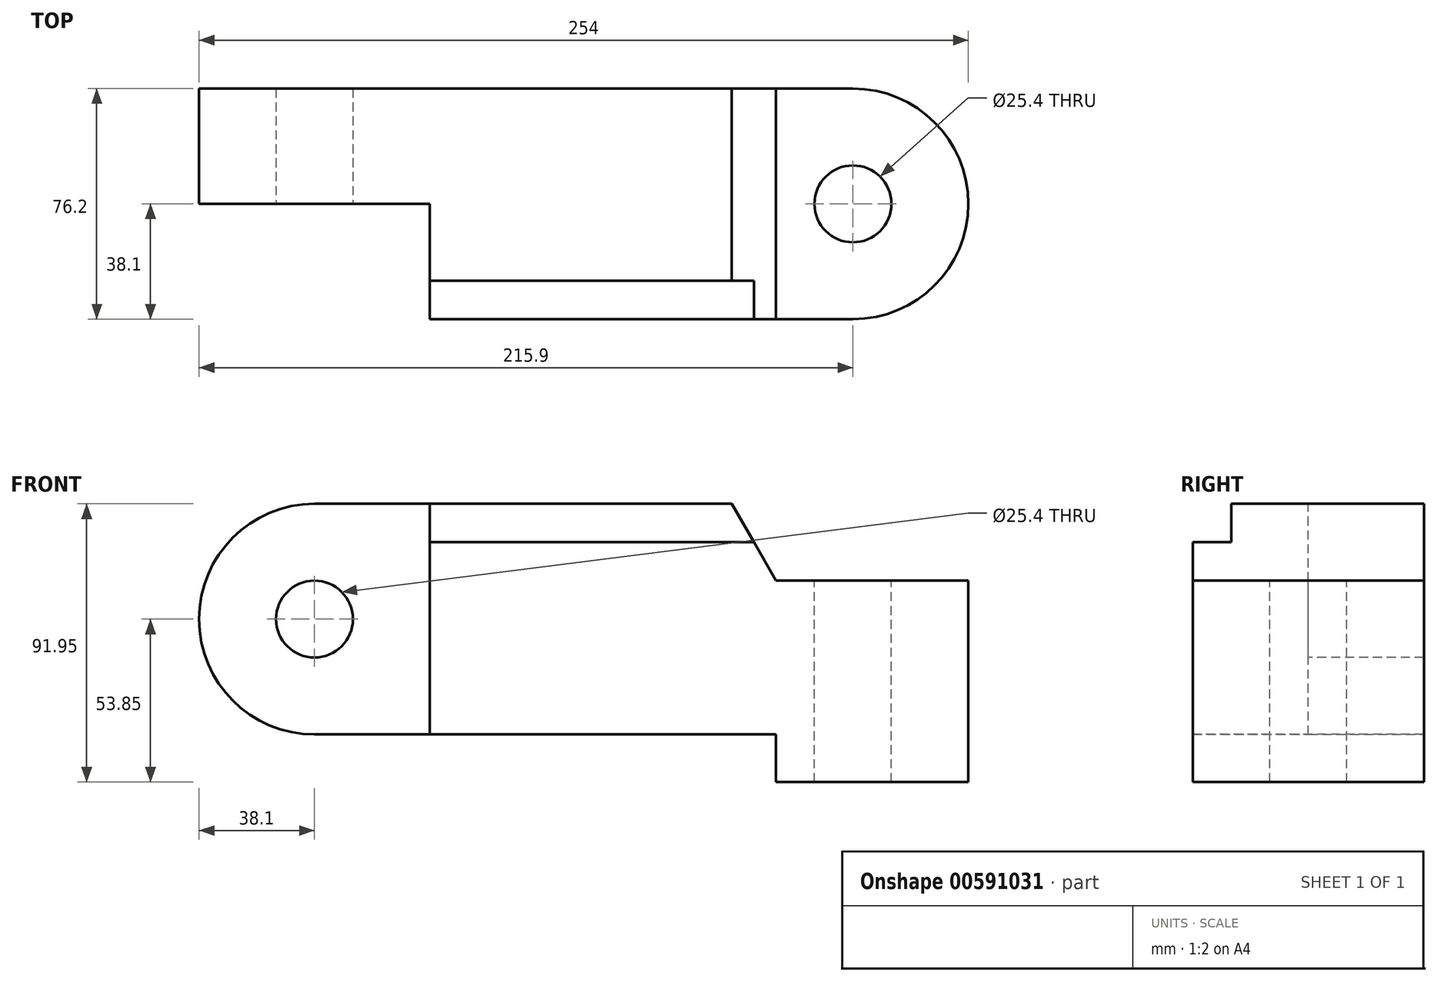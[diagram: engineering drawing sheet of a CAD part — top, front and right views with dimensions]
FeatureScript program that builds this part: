
annotation { "Feature Type Name" : "Feature", "Feature Type Description" : "" }
export const myFeature = defineFeature(function(context is Context, id is Id, definition is map)
    precondition{}
    {
        {
            var Q0;
            Q0=qCreatedBy(makeId("Top.planeOp"),FACE);
            var sketch = newSketch(context, id + "F0", { "sketchPlane" : qUnion([Q0])});
            skLineSegment(sketch, "E0.bottom", {"start": v(88.9, -38.1) * mm, "end": v(-88.9, -38.1) * mm});
            skLineSegment(sketch, "E0.top", {"start": v(88.9, 38.1) * mm, "end": v(-88.9, 38.1) * mm});
            skLineSegment(sketch, "E0.left", {"start": v(88.9, -38.1) * mm, "end": v(88.9, 38.1) * mm});
            skLineSegment(sketch, "E0.right", {"start": v(-88.9, -38.1) * mm, "end": v(-88.9, 38.1) * mm});
            skPoint(sketch, "E0.middle", {"position": v(0, 0) * mm});
            skSolve(sketch);
        }
        {
            var Q0;
            Q0=makeQuery(id+"F0.imprint","IMPRINT",FACE,{"disambiguationData":[TD([[makeQuery(id+"F0.imprint","IMPRINT",EDGE,{"derivedFrom":sQuery(id+"F0.wireOp",EDGE,"E0.bottom")}),-1.0]])]});
            extrude(context, id + "F1", {"entities" : qUnion([Q0]), "depth" : 76.2 * mm, "offsetDistance" : 25.4 * mm});
        }
        {
            var Q0;
            Q0=makeQuery(id+"F1.opExtrude","CAP_FACE",FACE,{"disambiguationData":[OSD([sQuery(id+"F0.wireOp",EDGE,"E0.bottom"),sQuery(id+"F0.wireOp",EDGE,"E0.top"),sQuery(id+"F0.wireOp",EDGE,"E0.left"),sQuery(id+"F0.wireOp",EDGE,"E0.right")])],"isStart":false});
            var sketch = newSketch(context, id + "F2", { "sketchPlane" : qUnion([Q0])});
            skLineSegment(sketch, "E1.bottom", {"start": v(-88.9, -38.1) * mm, "end": v(-50.8, -38.1) * mm});
            skLineSegment(sketch, "E1.top", {"start": v(-88.9, 0) * mm, "end": v(-50.8, 0) * mm});
            skLineSegment(sketch, "E1.left", {"start": v(-88.9, -38.1) * mm, "end": v(-88.9, 0) * mm});
            skLineSegment(sketch, "E1.right", {"start": v(-50.8, -38.1) * mm, "end": v(-50.8, 0) * mm});
            skSolve(sketch);
        }
        {
            var Q0;
            Q0=makeQuery(id+"F2.imprint","IMPRINT",FACE,{"disambiguationData":[TD([[makeQuery(id+"F2.imprint","IMPRINT",EDGE,{"derivedFrom":sQuery(id+"F2.wireOp",EDGE,"E1.bottom")}),-1.0]])]});
            extrude(context, id + "F3", {"entities" : qUnion([Q0]), "operationType" : NewBodyOperationType.REMOVE, "oppositeDirection" : true, "depth" : 76.2 * mm, "offsetDistance" : 25.4 * mm});
        }
        {
            var Q0;
            Q0=makeQuery(id+"F1.opExtrude","CAP_FACE",FACE,{"disambiguationData":[OSD([sQuery(id+"F0.wireOp",EDGE,"E0.bottom"),sQuery(id+"F0.wireOp",EDGE,"E0.top"),sQuery(id+"F0.wireOp",EDGE,"E0.left"),sQuery(id+"F0.wireOp",EDGE,"E0.right")])],"isStart":false});
            var sketch = newSketch(context, id + "F4", { "sketchPlane" : qUnion([Q0])});
            skLineSegment(sketch, "E2.bottom", {"start": v(88.9, -38.1) * mm, "end": v(63.5, -38.1) * mm});
            skLineSegment(sketch, "E2.top", {"start": v(88.9, 38.1) * mm, "end": v(63.5, 38.1) * mm});
            skLineSegment(sketch, "E2.left", {"start": v(88.9, -38.1) * mm, "end": v(88.9, 38.1) * mm});
            skLineSegment(sketch, "E2.right", {"start": v(63.5, -38.1) * mm, "end": v(63.5, 38.1) * mm});
            skSolve(sketch);
        }
        {
            var Q0;
            Q0=makeQuery(id+"F4.imprint","IMPRINT",FACE,{"disambiguationData":[TD([[makeQuery(id+"F4.imprint","IMPRINT",EDGE,{"derivedFrom":sQuery(id+"F4.wireOp",EDGE,"E2.bottom")}),-1.0]])]});
            extrude(context, id + "F5", {"entities" : qUnion([Q0]), "operationType" : NewBodyOperationType.REMOVE, "oppositeDirection" : true, "depth" : 25.4 * mm, "offsetDistance" : 25.4 * mm});
        }
        {
            var Q0;
            Q0=makeQuery(id+"F1.opExtrude","CAP_FACE",FACE,{"disambiguationData":[OSD([sQuery(id+"F0.wireOp",EDGE,"E0.bottom"),sQuery(id+"F0.wireOp",EDGE,"E0.top"),sQuery(id+"F0.wireOp",EDGE,"E0.left"),sQuery(id+"F0.wireOp",EDGE,"E0.right")])],"isStart":true});
            var sketch = newSketch(context, id + "F6", { "sketchPlane" : qUnion([Q0])});
            skLineSegment(sketch, "E3.bottom", {"start": v(88.9, -38.1) * mm, "end": v(63.5, -38.1) * mm});
            skLineSegment(sketch, "E3.top", {"start": v(88.9, 38.1) * mm, "end": v(63.5, 38.1) * mm});
            skLineSegment(sketch, "E3.left", {"start": v(88.9, -38.1) * mm, "end": v(88.9, 38.1) * mm});
            skLineSegment(sketch, "E3.right", {"start": v(63.5, -38.1) * mm, "end": v(63.5, 38.1) * mm});
            skSolve(sketch);
        }
        {
            var Q0;
            Q0=makeQuery(id+"F6.imprint","IMPRINT",FACE,{"disambiguationData":[TD([[makeQuery(id+"F6.imprint","IMPRINT",EDGE,{"derivedFrom":sQuery(id+"F6.wireOp",EDGE,"E3.bottom")}),-1.0]])]});
            extrude(context, id + "F7", {"entities" : qUnion([Q0]), "operationType" : NewBodyOperationType.ADD, "depth" : 15.75 * mm, "offsetDistance" : 25.4 * mm});
        }
        {
            var Q0;
            Q0=makeQuery(id+"F1.opExtrude","SWEPT_FACE",FACE,{"disambiguationData":[OSD([sQuery(id+"F0.wireOp",EDGE,"E0.right")])]});
            var sketch = newSketch(context, id + "F8", { "sketchPlane" : qUnion([Q0])});
            skLineSegment(sketch, "E4", {"start": v(-38.1, 38.1) * mm, "end": v(0, 38.1) * mm});
            skSolve(sketch);
        }
        {
            var Q0;
            {var subQ0=sQuery(id+"F8.wireOp",EDGE,"E4");Q0=makeQuery(id+"F8.imprint","IMPRINT",FACE,{"disambiguationData":[TD([[makeQuery(id+"F8.imprint","IMPRINT",EDGE,{"derivedFrom":subQ0}),1.0]])]});}
            var Q1;
            Q1=sQuery(id+"F8.wireOp",EDGE,"E4");
            revolve(context, id + "F9", {"operationType" : NewBodyOperationType.ADD, "entities" : qUnion([Q0]), "axis" : qUnion([Q1]), "revolveType" : RevolveType.FULL});
        }
        {
            var Q0;
            Q0=makeQuery(id+"F7.boolean.opBoolean","MERGE",FACE,{"derivedFrom":[makeQuery(id+"F1.opExtrude","SWEPT_FACE",FACE,{"disambiguationData":[OSD([sQuery(id+"F0.wireOp",EDGE,"E0.left")])]}),makeQuery(id+"F7.opExtrude","SWEPT_FACE",FACE,{"disambiguationData":[OSD([sQuery(id+"F6.wireOp",EDGE,"E3.left")])]})]});
            var sketch = newSketch(context, id + "F10", { "sketchPlane" : qUnion([Q0])});
            skLineSegment(sketch, "E5", {"start": v(0, 50.8) * mm, "end": v(0, -15.75) * mm});
            skSolve(sketch);
        }
        {
            var Q0;
            {var subQ0=sQuery(id+"F10.wireOp",EDGE,"E5");Q0=makeQuery(id+"F10.imprint","IMPRINT",FACE,{"disambiguationData":[TD([[makeQuery(id+"F10.imprint","IMPRINT",EDGE,{"derivedFrom":subQ0}),1.0]])]});}
            var Q1;
            Q1=sQuery(id+"F10.wireOp",EDGE,"E5");
            revolve(context, id + "F11", {"operationType" : NewBodyOperationType.ADD, "entities" : qUnion([Q0]), "axis" : qUnion([Q1]), "revolveType" : RevolveType.FULL});
        }
        {
            var Q0;
            Q0=makeQuery(id+"F7.boolean.opBoolean","MERGE",FACE,{"derivedFrom":[makeQuery(id+"F1.opExtrude","SWEPT_FACE",FACE,{"disambiguationData":[OSD([sQuery(id+"F0.wireOp",EDGE,"E0.bottom")])]}),makeQuery(id+"F7.opExtrude","SWEPT_FACE",FACE,{"disambiguationData":[OSD([sQuery(id+"F6.wireOp",EDGE,"E3.top")])]})]});
            var sketch = newSketch(context, id + "F12", { "sketchPlane" : qUnion([Q0])});
            skLineSegment(sketch, "E6", {"start": v(63.5, 50.8) * mm, "end": v(48.84, 76.2) * mm});
            skSolve(sketch);
        }
        {
            var Q0;
            Q0 = qSketchRegion(id + "F12", true);
            var Q1;
            {var subQ0=sQuery(id+"F12.wireOp",EDGE,"E6");Q1=makeQuery(id+"F12.imprint","IMPRINT",FACE,{"disambiguationData":[TD([[makeQuery(id+"F12.imprint","IMPRINT",EDGE,{"derivedFrom":subQ0}),-1.0]])]});}
            extrude(context, id + "F13", {"entities" : qUnion([Q0, Q1]), "operationType" : NewBodyOperationType.REMOVE, "oppositeDirection" : true, "depth" : 76.2 * mm, "offsetDistance" : 25.4 * mm});
        }
        {
            var Q0;
            {var subQ0=sQuery(id+"F4.wireOp",EDGE,"E2.left");Q0=makeQuery(id+"F11.boolean.opBoolean","MERGE",FACE,{"derivedFrom":[makeQuery(id+"F5.boolean.opBoolean","COPY",FACE,{"derivedFrom":makeQuery(id+"F5.opExtrude","CAP_FACE",FACE,{"disambiguationData":[OSD([sQuery(id+"F4.wireOp",EDGE,"E2.bottom"),sQuery(id+"F4.wireOp",EDGE,"E2.top"),subQ0,sQuery(id+"F4.wireOp",EDGE,"E2.right")])],"isStart":false})}),makeQuery(id+"F11.opRevolve","SWEPT_FACE",FACE,{"disambiguationData":[OSD([subQ0])]})]});}
            var sketch = newSketch(context, id + "F14", { "sketchPlane" : qUnion([Q0])});
            skLineSegment(sketch, "E7.bottom", {"start": v(63.5, -38.1) * mm, "end": v(88.9, -38.1) * mm});
            skLineSegment(sketch, "E7.top", {"start": v(63.5, 0) * mm, "end": v(88.9, 0) * mm});
            skLineSegment(sketch, "E7.left", {"start": v(63.5, -38.1) * mm, "end": v(63.5, 0) * mm});
            skLineSegment(sketch, "E7.right", {"start": v(88.9, -38.1) * mm, "end": v(88.9, 0) * mm});
            skCircle(sketch, "E8", {"center": v(88.9, 0) * mm, "radius": 12.7 * mm});
            skSolve(sketch);
        }
        {
            var Q0;
            {var subQ0=sQuery(id+"F14.wireOp",EDGE,"E7.right");var subQ1=sQuery(id+"F14.wireOp",EDGE,"E7.top");var subQ2=makeQuery(id+"F14.imprint","INTERSECT",VERTEX,{"derivedFrom":[subQ1,subQ0]});Q0=makeQuery(id+"F14.imprint","IMPRINT",FACE,{"disambiguationData":[TD([[makeQuery(id+"F14.imprint","IMPRINT",EDGE,{"disambiguationData":[TD([[subQ2,1.0]])],"derivedFrom":subQ1}),-1.0]])]});}
            var Q1;
            {var subQ0=sQuery(id+"F14.wireOp",EDGE,"E7.right");var subQ1=sQuery(id+"F14.wireOp",EDGE,"E7.top");var subQ2=makeQuery(id+"F14.imprint","INTERSECT",VERTEX,{"derivedFrom":[subQ1,subQ0]});Q1=makeQuery(id+"F14.imprint","IMPRINT",FACE,{"disambiguationData":[TD([[makeQuery(id+"F14.imprint","IMPRINT",EDGE,{"disambiguationData":[TD([[subQ2,1.0]])],"derivedFrom":subQ1}),1.0]])]});}
            extrude(context, id + "F15", {"entities" : qUnion([Q0, Q1]), "operationType" : NewBodyOperationType.REMOVE, "oppositeDirection" : true, "depth" : 101.6 * mm, "offsetDistance" : 25.4 * mm});
        }
        {
            var Q0;
            {var subQ0=sQuery(id+"F6.wireOp",EDGE,"E3.left");Q0=makeQuery(id+"F11.boolean.opBoolean","MERGE",FACE,{"derivedFrom":[makeQuery(id+"F7.opExtrude","CAP_FACE",FACE,{"disambiguationData":[OSD([sQuery(id+"F6.wireOp",EDGE,"E3.bottom"),sQuery(id+"F6.wireOp",EDGE,"E3.top"),subQ0,sQuery(id+"F6.wireOp",EDGE,"E3.right")])],"isStart":false}),makeQuery(id+"F11.opRevolve","SWEPT_FACE",FACE,{"disambiguationData":[OSD([subQ0])]})]});}
            var sketch = newSketch(context, id + "F16", { "sketchPlane" : qUnion([Q0])});
            skLineSegment(sketch, "E9", {"start": v(63.5, 28.4) * mm, "end": v(63.5, -28.4) * mm});
            skSolve(sketch);
        }
        {
            var Q0;
            Q0=makeQuery(id+"F16.imprint","IMPRINT",FACE,{"disambiguationData":[TD([[makeQuery(id+"F16.imprint","IMPRINT",EDGE,{"derivedFrom":sQuery(id+"F16.wireOp",EDGE,"E9")}),-1.0]])]});
            extrude(context, id + "F17", {"entities" : qUnion([Q0]), "operationType" : NewBodyOperationType.REMOVE, "oppositeDirection" : true, "depth" : 15.75 * mm, "offsetDistance" : 25.4 * mm});
        }
        {
            var Q0;
            {var subQ0=sQuery(id+"F2.wireOp",EDGE,"E1.top");Q0=makeQuery(id+"F9.boolean.opBoolean","MERGE",FACE,{"derivedFrom":[makeQuery(id+"F3.boolean.opBoolean","COPY",FACE,{"derivedFrom":makeQuery(id+"F3.opExtrude","SWEPT_FACE",FACE,{"disambiguationData":[OSD([subQ0])]})}),makeQuery(id+"F9.opRevolve","SWEPT_FACE",FACE,{"disambiguationData":[OSD([sQuery(id+"F0.wireOp",EDGE,"E0.right"),subQ0,sQuery(id+"F2.wireOp",EDGE,"E1.left")])]})]});}
            var sketch = newSketch(context, id + "F18", { "sketchPlane" : qUnion([Q0])});
            skLineSegment(sketch, "E10.bottom", {"start": v(-50.8, 76.2) * mm, "end": v(-88.9, 76.2) * mm});
            skLineSegment(sketch, "E10.top", {"start": v(-50.8, 38.1) * mm, "end": v(-88.9, 38.1) * mm});
            skLineSegment(sketch, "E10.left", {"start": v(-50.8, 76.2) * mm, "end": v(-50.8, 38.1) * mm});
            skLineSegment(sketch, "E10.right", {"start": v(-88.9, 76.2) * mm, "end": v(-88.9, 38.1) * mm});
            skCircle(sketch, "E11", {"center": v(-88.9, 38.1) * mm, "radius": 12.7 * mm});
            skSolve(sketch);
        }
        {
            var Q0;
            {var subQ0=sQuery(id+"F18.wireOp",EDGE,"E10.right");var subQ1=sQuery(id+"F18.wireOp",EDGE,"E10.top");var subQ2=makeQuery(id+"F18.imprint","INTERSECT",VERTEX,{"derivedFrom":[subQ1,subQ0]});Q0=makeQuery(id+"F18.imprint","IMPRINT",FACE,{"disambiguationData":[TD([[makeQuery(id+"F18.imprint","IMPRINT",EDGE,{"disambiguationData":[TD([[subQ2,1.0]])],"derivedFrom":subQ1}),-1.0]])]});}
            var Q1;
            {var subQ0=sQuery(id+"F18.wireOp",EDGE,"E10.right");var subQ1=sQuery(id+"F18.wireOp",EDGE,"E10.top");var subQ2=makeQuery(id+"F18.imprint","INTERSECT",VERTEX,{"derivedFrom":[subQ1,subQ0]});Q1=makeQuery(id+"F18.imprint","IMPRINT",FACE,{"disambiguationData":[TD([[makeQuery(id+"F18.imprint","IMPRINT",EDGE,{"disambiguationData":[TD([[subQ2,1.0]])],"derivedFrom":subQ1}),1.0]])]});}
            extrude(context, id + "F19", {"entities" : qUnion([Q0, Q1]), "operationType" : NewBodyOperationType.REMOVE, "oppositeDirection" : true, "depth" : 38.1 * mm, "offsetDistance" : 25.4 * mm});
        }
        {
            var Q0;
            Q0=makeQuery(id+"F3.boolean.opBoolean","COPY",FACE,{"derivedFrom":makeQuery(id+"F3.opExtrude","SWEPT_FACE",FACE,{"disambiguationData":[OSD([sQuery(id+"F2.wireOp",EDGE,"E1.right")])]})});
            var sketch = newSketch(context, id + "F20", { "sketchPlane" : qUnion([Q0])});
            skLineSegment(sketch, "E12.bottom", {"start": v(38.1, 76.2) * mm, "end": v(25.4, 76.2) * mm});
            skLineSegment(sketch, "E12.top", {"start": v(38.1, 63.5) * mm, "end": v(25.4, 63.5) * mm});
            skLineSegment(sketch, "E12.left", {"start": v(38.1, 76.2) * mm, "end": v(38.1, 63.5) * mm});
            skLineSegment(sketch, "E12.right", {"start": v(25.4, 76.2) * mm, "end": v(25.4, 63.5) * mm});
            skSolve(sketch);
        }
        {
            var Q0;
            Q0 = qSketchRegion(id + "F20", true);
            extrude(context, id + "F21", {"entities" : qUnion([Q0]), "operationType" : NewBodyOperationType.REMOVE, "oppositeDirection" : true, "depth" : 127 * mm, "offsetDistance" : 25.4 * mm});
        }
    });
